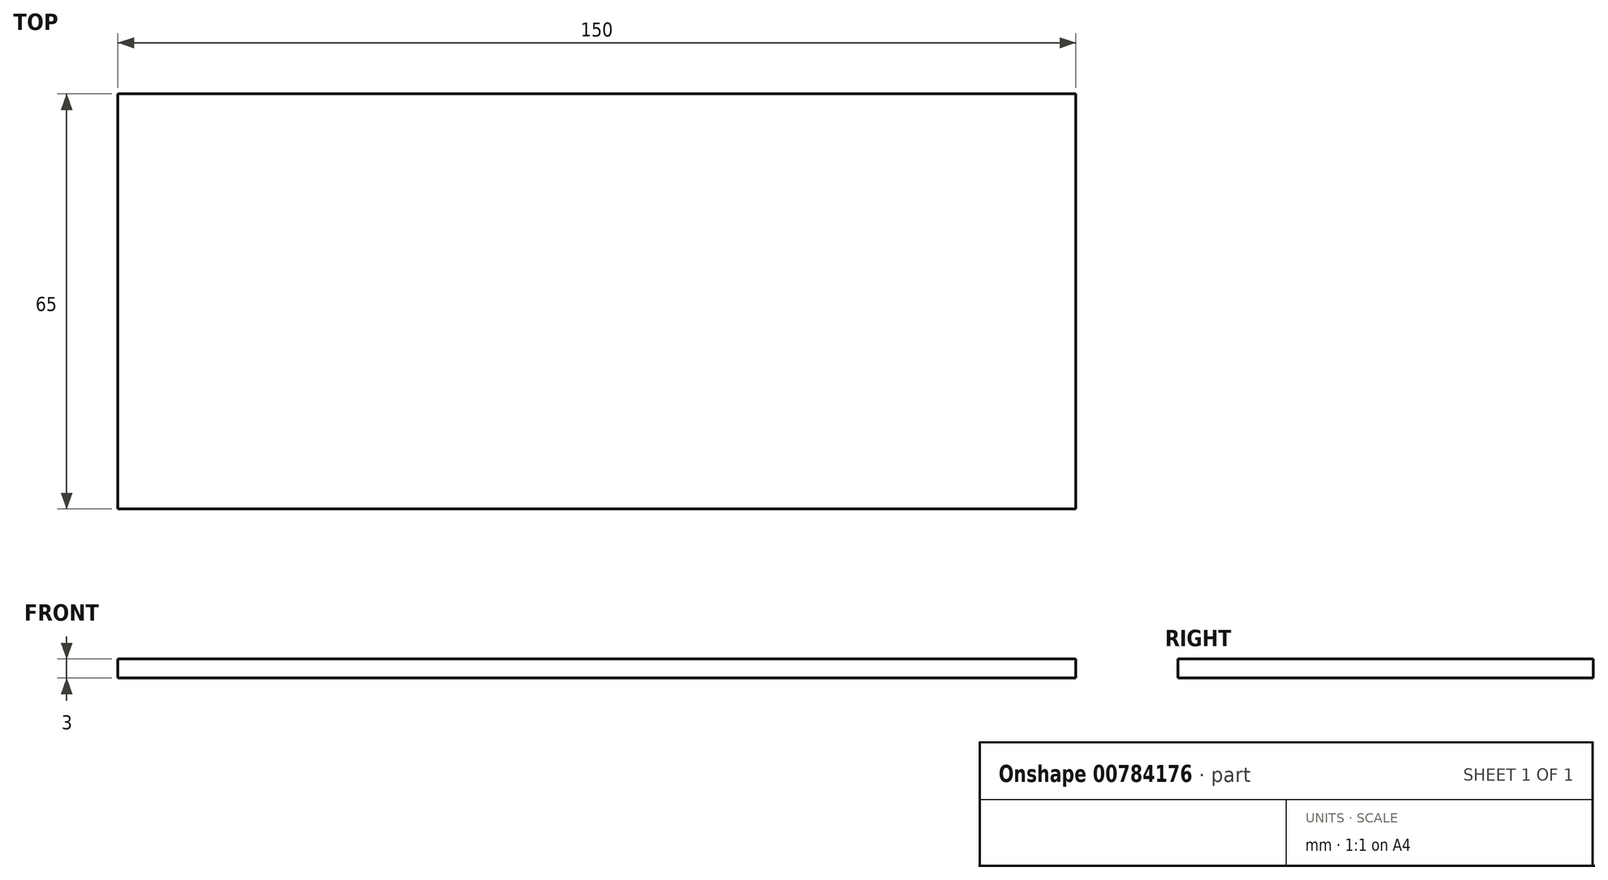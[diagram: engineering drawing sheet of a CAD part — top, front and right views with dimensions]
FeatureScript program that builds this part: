
annotation { "Feature Type Name" : "Feature", "Feature Type Description" : "" }
export const myFeature = defineFeature(function(context is Context, id is Id, definition is map)
    precondition{}
    {
        {
            var Q0;
            Q0=qCreatedBy(makeId("Top.planeOp"),FACE);
            var sketch = newSketch(context, id + "F0", { "sketchPlane" : qUnion([Q0])});
            skLineSegment(sketch, "E0.bottom", {"start": v(75, 32.5) * mm, "end": v(-75, 32.5) * mm});
            skLineSegment(sketch, "E0.top", {"start": v(75, -32.5) * mm, "end": v(-75, -32.5) * mm});
            skLineSegment(sketch, "E0.left", {"start": v(75, 32.5) * mm, "end": v(75, -32.5) * mm});
            skLineSegment(sketch, "E0.right", {"start": v(-75, 32.5) * mm, "end": v(-75, -32.5) * mm});
            skPoint(sketch, "E0.middle", {"position": v(0, 0) * mm});
            skSolve(sketch);
        }
        {
            var Q0;
            Q0 = qSketchRegion(id + "F0", true);
            extrude(context, id + "F1", {"entities" : qUnion([Q0]), "depth" : 3 * mm, "offsetDistance" : 25 * mm});
        }
    });
